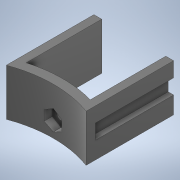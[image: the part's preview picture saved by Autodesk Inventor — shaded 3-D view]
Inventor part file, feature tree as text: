
AUTODESK INVENTOR PART (.ipt)
format: ipt  version: 2020 (Build 240168000, 168)  size: 305,152 bytes
history: native  units: mm
features: extrude x6, projected_geometry x5, sketch x4, other x3
ambient origin geometry x8: Origin, YZ Plane, XZ Plane, XY Plane, X Axis, Y Axis, Z Axis, Center Point
bodies: Body1 (feature_tree)
feature tree (18):
  extrude  "Выдавливание7"  Depth=4.0mm
  other  "РабПлоскость1"
  sketch  "Эскиз6"
  extrude  "Выдавливание8"  Depth=25.5mm
  sketch  "Эскиз7"
  other  "РабПлоскость2"
  sketch  "Эскиз8"
  other  "РабПлоскость3"
  extrude  "Выдавливание12"  Depth=3.0mm
  extrude  "Выдавливание13"  Depth=3.0mm
  extrude  "Выдавливание15"  Depth=3.0mm
  extrude  "Выдавливание14"  Depth=20.2mm
  sketch  "Эскиз1"
  projected_geometry  "Спроецированная петля4"
  projected_geometry  "Спроецированная петля5"
  projected_geometry  "Спроецированная петля6"
  projected_geometry  "Спроецированная петля7"
  projected_geometry  "Спроецированная петля8"
